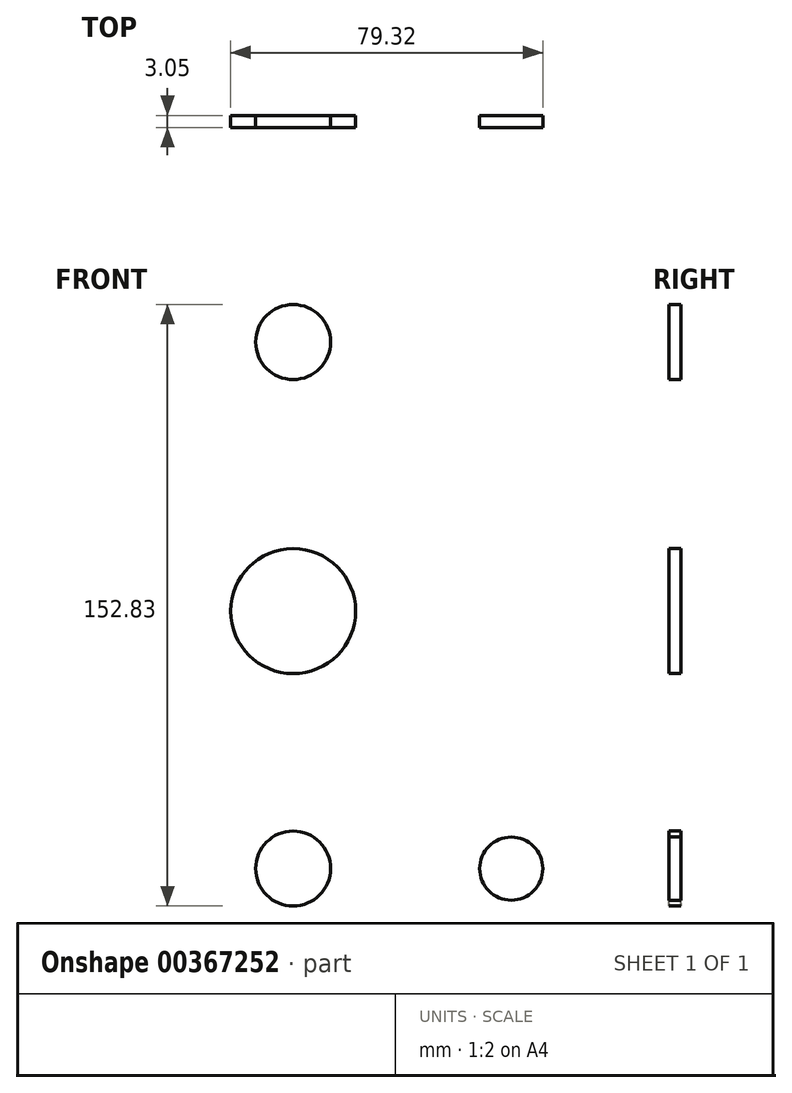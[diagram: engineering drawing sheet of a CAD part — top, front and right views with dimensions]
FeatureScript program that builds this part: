
annotation { "Feature Type Name" : "Feature", "Feature Type Description" : "" }
export const myFeature = defineFeature(function(context is Context, id is Id, definition is map)
    precondition{}
    {
        {
            var Q0;
            Q0=qCreatedBy(makeId("Front.planeOp"),FACE);
            var sketch = newSketch(context, id + "F0", { "sketchPlane" : qUnion([Q0])});
            skCircle(sketch, "E0", {"center": v(0, -65.42) * mm, "radius": 9.53 * mm});
            skCircle(sketch, "E1", {"center": v(0, 0) * mm, "radius": 15.88 * mm});
            skCircle(sketch, "E2", {"center": v(0, 68.36) * mm, "radius": 9.53 * mm});
            skLineSegment(sketch, "E3", {"start": v(0, 68.36) * mm, "end": v(0, -65.42) * mm});
            skLineSegment(sketch, "E4", {"start": v(0, -65.42) * mm, "end": v(62.3, -65.42) * mm});
            skCircle(sketch, "E5", {"center": v(55.42, -65.42) * mm, "radius": 8.02 * mm});
            skSolve(sketch);
        }
        {
            var Q0;
            Q0 = qSketchRegion(id + "F0", true);
            extrude(context, id + "F1", {"entities" : qUnion([Q0]), "depth" : 3.05 * mm});
        }
    });
